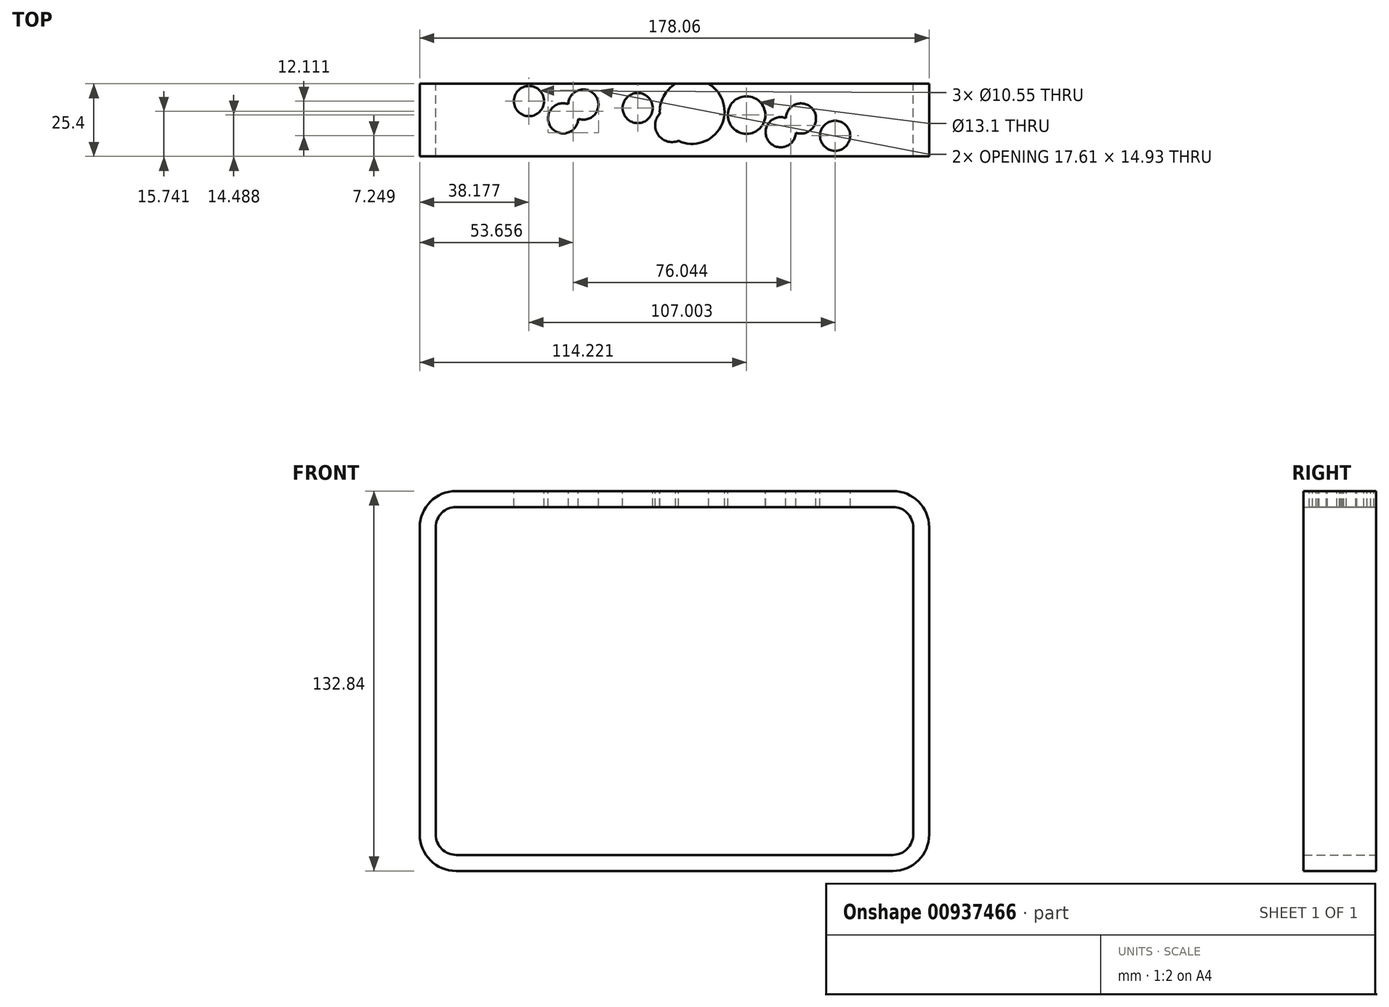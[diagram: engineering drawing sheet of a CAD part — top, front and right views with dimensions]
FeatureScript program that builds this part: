
annotation { "Feature Type Name" : "Feature", "Feature Type Description" : "" }
export const myFeature = defineFeature(function(context is Context, id is Id, definition is map)
    precondition{}
    {
        {
            var Q0;
            Q0=qCreatedBy(makeId("Front.planeOp"),FACE);
            var sketch = newSketch(context, id + "F0", { "sketchPlane" : qUnion([Q0])});
            skLineSegment(sketch, "E0.bottom", {"start": v(-76.33, 66.42) * mm, "end": v(76.33, 66.42) * mm});
            skLineSegment(sketch, "E0.top", {"start": v(-76.33, -66.42) * mm, "end": v(76.33, -66.42) * mm});
            skLineSegment(sketch, "E0.left", {"start": v(-89.03, 53.72) * mm, "end": v(-89.03, -53.72) * mm});
            skLineSegment(sketch, "E0.right", {"start": v(89.03, 53.72) * mm, "end": v(89.03, -53.72) * mm});
            skPoint(sketch, "E0.middle", {"position": v(0, 0) * mm});
            skPoint(sketch, "E1.visualSharp", {"position": v(-89.03, 66.42) * mm});
            skArc(sketch, "E1.filletArc", {"start": v(-76.33, 66.42) * mm, "mid": v(-85.3, 62.7) * mm, "end": v(-89.03, 53.72) * mm});
            skPoint(sketch, "E2.visualSharp", {"position": v(89.03, 66.42) * mm});
            skArc(sketch, "E2.filletArc", {"start": v(89.03, 53.72) * mm, "mid": v(85.3, 62.7) * mm, "end": v(76.33, 66.42) * mm});
            skPoint(sketch, "E3.visualSharp", {"position": v(89.03, -66.42) * mm});
            skArc(sketch, "E3.filletArc", {"start": v(76.33, -66.42) * mm, "mid": v(85.3, -62.7) * mm, "end": v(89.03, -53.72) * mm});
            skPoint(sketch, "E4.visualSharp", {"position": v(-89.03, -66.42) * mm});
            skArc(sketch, "E4.filletArc", {"start": v(-89.03, -53.72) * mm, "mid": v(-85.3, -62.7) * mm, "end": v(-76.33, -66.42) * mm});
            skArc(sketch, "E5.0", {"start": v(-76.33, 60.83) * mm, "mid": v(-81.36, 58.75) * mm, "end": v(-83.44, 53.72) * mm});
            skLineSegment(sketch, "E5.1", {"start": v(-83.44, 53.72) * mm, "end": v(-83.44, -53.72) * mm});
            skLineSegment(sketch, "E5.2", {"start": v(-76.33, 60.83) * mm, "end": v(76.33, 60.83) * mm});
            skArc(sketch, "E5.3", {"start": v(-83.44, -53.72) * mm, "mid": v(-81.36, -58.75) * mm, "end": v(-76.33, -60.83) * mm});
            skArc(sketch, "E5.4", {"start": v(83.44, 53.72) * mm, "mid": v(81.36, 58.75) * mm, "end": v(76.33, 60.83) * mm});
            skLineSegment(sketch, "E5.5", {"start": v(83.44, 53.72) * mm, "end": v(83.44, -53.72) * mm});
            skArc(sketch, "E5.6", {"start": v(76.33, -60.83) * mm, "mid": v(81.36, -58.75) * mm, "end": v(83.44, -53.72) * mm});
            skLineSegment(sketch, "E5.7", {"start": v(-76.33, -60.83) * mm, "end": v(76.33, -60.83) * mm});
            skLineSegment(sketch, "E6", {"start": v(-87.82, -106.3) * mm, "end": v(31.8, -106.3) * mm});
            skSolve(sketch);
        }
        {
            var Q0;
            Q0 = qSketchRegion(id + "F0", true);
            extrude(context, id + "F1", {"entities" : qUnion([Q0]), "depth" : 25.4 * mm, "offsetDistance" : 25.4 * mm});
        }
        {
            var Q0;
            Q0=makeQuery(id+"F1.opExtrude","SWEPT_FACE",FACE,{"disambiguationData":[OSD([sQuery(id+"F0.wireOp",EDGE,"E0.bottom")])]});
            var sketch = newSketch(context, id + "F2", { "sketchPlane" : qUnion([Q0])});
            skCircle(sketch, "E7", {"center": v(44.2, -12.13) * mm, "radius": 5.27 * mm});
            skCircle(sketch, "E8.0.1.0", {"center": v(56.15, -18.15) * mm, "radius": 5.27 * mm});
            skCircle(sketch, "E8.1.0.0", {"center": v(25.2, -10.91) * mm, "radius": 6.55 * mm});
            skCircle(sketch, "E8.1.1.0", {"center": v(37.14, -16.93) * mm, "radius": 5.27 * mm});
            skCircle(sketch, "E8.2.0.0", {"center": v(6.18, -9.7) * mm, "radius": 11.3 * mm});
            skCircle(sketch, "E8.3.0.0", {"center": v(-12.83, -8.48) * mm, "radius": 5.27 * mm});
            skCircle(sketch, "E8.3.1.0", {"center": v(-0.88, -14.5) * mm, "radius": 5.87 * mm});
            skCircle(sketch, "E8.4.0.0", {"center": v(-31.84, -7.26) * mm, "radius": 5.27 * mm});
            skCircle(sketch, "E8.5.0.0", {"center": v(-50.85, -6.04) * mm, "radius": 5.27 * mm});
            skCircle(sketch, "E8.5.1.0", {"center": v(-38.9, -12.06) * mm, "radius": 5.27 * mm});
            skLineSegment(sketch, "E8.direction1", {"start": v(44.2, -12.13) * mm, "end": v(25.2, -10.91) * mm, "construction": true});
            skLineSegment(sketch, "E8.direction2", {"start": v(44.2, -12.13) * mm, "end": v(56.15, -18.15) * mm, "construction": true});
            skSolve(sketch);
        }
        {
            var Q0;
            Q0 = qSketchRegion(id + "F2", true);
            extrude(context, id + "F3", {"entities" : qUnion([Q0]), "operationType" : NewBodyOperationType.REMOVE, "oppositeDirection" : true, "depth" : 25.4 * mm, "offsetDistance" : 25.4 * mm});
        }
    });
